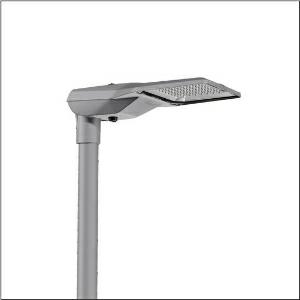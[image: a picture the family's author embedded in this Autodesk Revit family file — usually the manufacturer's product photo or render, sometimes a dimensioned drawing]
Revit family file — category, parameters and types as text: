
# Revit family: streetlight_sl_21_midi___st0_5a_5xe3b33t08mb_6d0d
name_source: partatom
category: Lighting Fixtures
units: mm (PartAtom-declared; Revit-internal decimal feet)

## family parameters
Cut with Voids When Loaded = No
Host = Face
Light Source = No
Part Type = Normal
Room Calculation Point = No
Round Connector Dimension = Use Diameter
Shared = No

## types (1)
- --- (1 x LED, 18270 lm, 136 W, 3000K)
    Apparent Load = 136 VA
    CIE Flux Codes = 41 75 97 100 100
    Color Rendering = 70
    Color Temperature = 3000K
    Default Elevation = 1800 mm
    Description = Streetlight SL 21 midi, mast luminaire, primary light control with lens, of PMMA, primary optical cover: cover, of toughened safety glass, transparent, light distribution: ST0.5a, light emission: direct distribution, primary light characteristic: asymmetric, installation type: side-entry, post-top, LED, High Power LED, rated luminous flux: 18.270lm, luminous efficacy: 134lm/W, light colour: 730, colour temperature: 3000K, control gear: D4i, control: overheat protection, constant luminous flux control, time-dependent luminous flux control, flexible luminous flux parameterisation, pre-setting: logarithmic dimming characteristic, mains connection: 230..240V, AC, 50/60Hz, start of lifetime: 136W, end of service life: 142W, reduction: 61W, luminaire housing, of diecast aluminium, powder-coated, SITECO metallic grey (DB 702S), corrosivity category C5 high according to DIN EN ISO 12944, please order mast flange separately, inclination adjustable: 0°, 5°, 10°, 15°, sealing non-destructively replaceable, multi-level sealing system, length: 644mm, width: 335mm, height: 110mm, mast flange for spigot size: 42mm (side-entry): 5XC10008XM4, 60/48mm (side-entry/post-top): 5XC10108XM2, 76/60mm (side-entry/post-top): 5XC10108XM1, mounting height: 4..8m, Smart Interface below and above, protection rating (complete): IP66, insulation class (complete): insulation class II (safety insulation), certification: CE, ENEC, ENEC+, VDE, impact resistance: IK10, permissible operating ambient temperature for outdoor applications: -40..+50°C, standard-compliant lighting for roads and squares, packaging unit: 1 piece

Light Distribution: ST0.5a
    Height = 111 mm
    Lamp = 1 x LED
    Lamp Light Flux = 18270 lm
    Lamp Power = 136 W
    Lamp count = 1
    Length = 644 mm
    Luminous efficacy = 134 lm/W
    Manufacturer = Siteco
    ModVariant = No
    Model = 5XE3B33T08MB
    Number of Poles = 1
    OnlyDefault = Yes
    Power Factor = 1
    Product Name = Streetlight SL 21 midi | ST0.5a
    Product group = mast luminaire | pylon top
    ProductGroupID = 6100
    Protection Class = Protection class II
    Protection Degree = IP 66
    RLX_Detail_Level = 1
    RLX_Emergency_Light_Flux = 0 lm
    RLX_Emergency_Type = 0
    RLX_Emergency_Type_DB = No
    RlxData = <blob elided: 37953 chars, md5=87c321a4>
    Socket = socket
    Standby Power = 0 W
    System Light Flux = 18270 lm
    System Power = 136 W
    Type Comments = factory setting: luminous flux: 100 % | dim-lin: 254 | 695 mA
    Type Image = l_1004304.jpg
    URL = http://relux.com
    VarID = @adj_189109
    Voltage = 0 V
    Weight = 0.00 kg
    Width = 336 mm

## geometry (parser evidence)
native form markers: Blend x4, Sweep x11
no freeform markers — native parametric forms only
